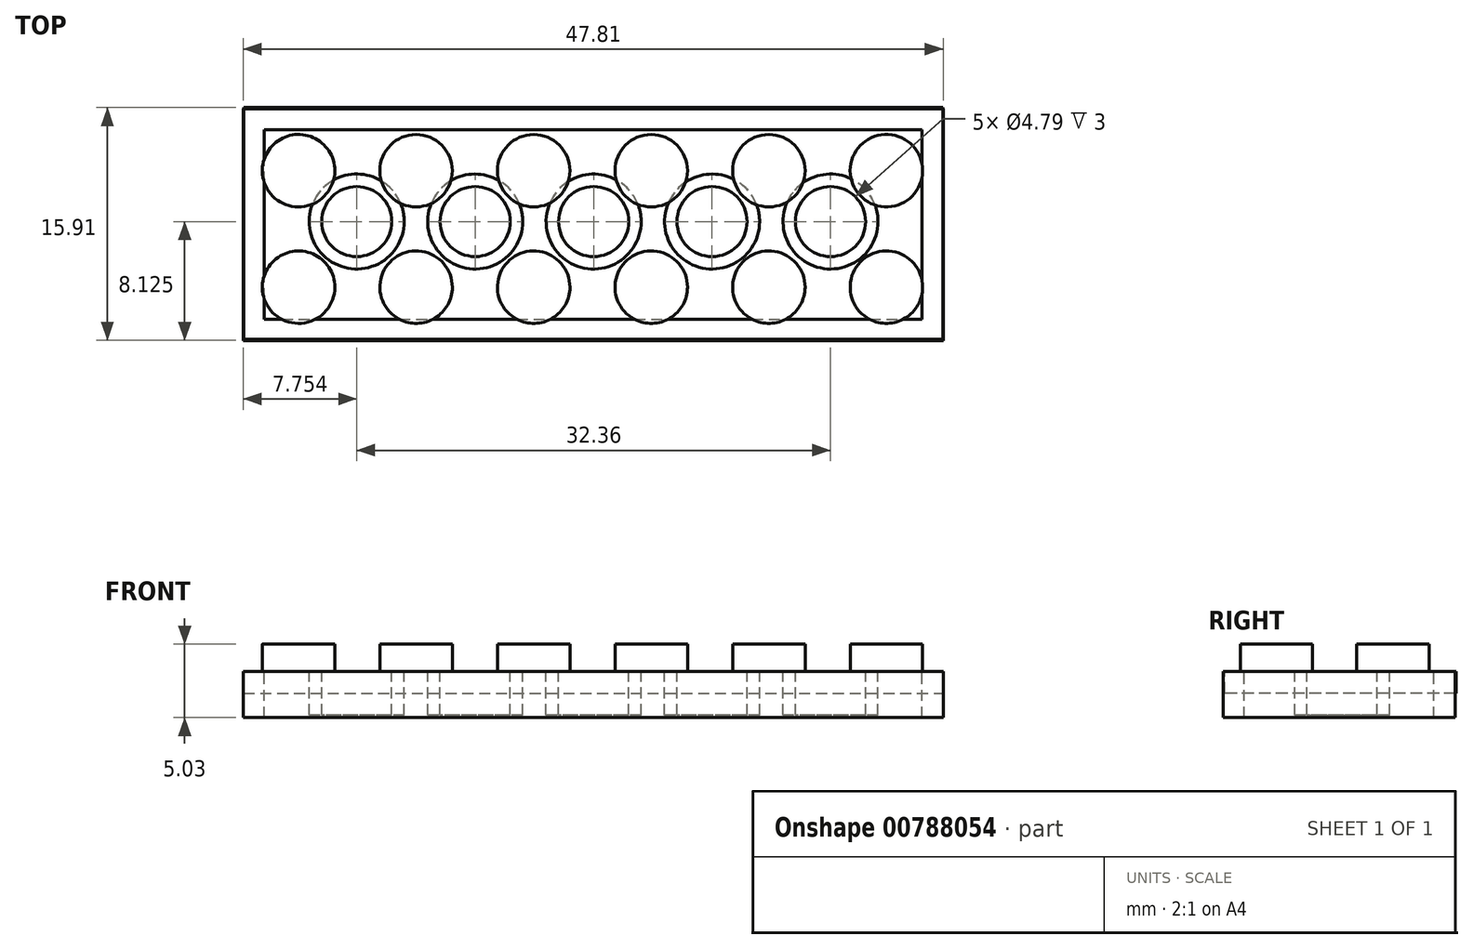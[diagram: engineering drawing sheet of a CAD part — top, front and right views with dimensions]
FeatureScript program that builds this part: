
annotation { "Feature Type Name" : "Feature", "Feature Type Description" : "" }
export const myFeature = defineFeature(function(context is Context, id is Id, definition is map)
    precondition{}
    {
        {
            var Q0;
            Q0=qCreatedBy(makeId("Top.planeOp"),FACE);
            var sketch = newSketch(context, id + "F0", { "sketchPlane" : qUnion([Q0])});
            skLineSegment(sketch, "E0.bottom", {"start": v(-44.16, 3.14) * mm, "end": v(3.65, 3.14) * mm});
            skLineSegment(sketch, "E0.top", {"start": v(-44.16, -12.7) * mm, "end": v(3.65, -12.7) * mm});
            skLineSegment(sketch, "E0.left", {"start": v(-44.16, 3.14) * mm, "end": v(-44.16, -12.7) * mm});
            skLineSegment(sketch, "E0.right", {"start": v(3.65, 3.14) * mm, "end": v(3.65, -12.7) * mm});
            skSolve(sketch);
        }
        {
            var Q0;
            Q0 = qSketchRegion(id + "F0", true);
            extrude(context, id + "F1", {"entities" : qUnion([Q0]), "oppositeDirection" : true, "depth" : 3.17 * mm, "offsetDistance" : 25 * mm});
        }
        {
            var Q0;
            Q0=qCreatedBy(makeId("Top.planeOp"),FACE);
            var sketch = newSketch(context, id + "F2", { "sketchPlane" : qUnion([Q0])});
            skCircle(sketch, "E1", {"center": v(-40.38, -1.1) * mm, "radius": 2.48 * mm});
            skCircle(sketch, "E2", {"center": v(-32.35, -1.1) * mm, "radius": 2.48 * mm});
            skCircle(sketch, "E3", {"center": v(-24.32, -1.1) * mm, "radius": 2.48 * mm});
            skCircle(sketch, "E4", {"center": v(-16.29, -1.1) * mm, "radius": 2.48 * mm});
            skCircle(sketch, "E5", {"center": v(-8.26, -1.1) * mm, "radius": 2.48 * mm});
            skCircle(sketch, "E6", {"center": v(-0.23, -1.1) * mm, "radius": 2.48 * mm});
            skCircle(sketch, "E7", {"center": v(-40.38, -9.06) * mm, "radius": 2.48 * mm});
            skCircle(sketch, "E8", {"center": v(-32.35, -9.06) * mm, "radius": 2.48 * mm});
            skCircle(sketch, "E9", {"center": v(-24.32, -9.06) * mm, "radius": 2.48 * mm});
            skCircle(sketch, "E10", {"center": v(-16.29, -9.06) * mm, "radius": 2.48 * mm});
            skCircle(sketch, "E11", {"center": v(-8.26, -9.06) * mm, "radius": 2.48 * mm});
            skCircle(sketch, "E12", {"center": v(-0.23, -9.06) * mm, "radius": 2.48 * mm});
            skSolve(sketch);
        }
        {
            var Q0;
            Q0 = qSketchRegion(id + "F2", true);
            extrude(context, id + "F3", {"entities" : qUnion([Q0]), "operationType" : NewBodyOperationType.ADD, "depth" : 1.86 * mm, "offsetDistance" : 25 * mm});
        }
        {
            var Q0;
            Q0=qCreatedBy(makeId("Top.planeOp"),FACE);
            var sketch = newSketch(context, id + "F4", { "sketchPlane" : qUnion([Q0])});
            skLineSegment(sketch, "E13.top", {"start": v(-42.71, -11.25) * mm, "end": v(2.2, -11.25) * mm});
            skLineSegment(sketch, "E14", {"start": v(-42.71, -11.25) * mm, "end": v(-42.71, 1.69) * mm});
            skLineSegment(sketch, "E15", {"start": v(-42.71, 1.69) * mm, "end": v(2.2, 1.69) * mm});
            skLineSegment(sketch, "E16", {"start": v(2.2, 1.69) * mm, "end": v(2.2, -11.25) * mm});
            skSolve(sketch);
        }
        {
            var Q0;
            Q0 = qSketchRegion(id + "F4", true);
            extrude(context, id + "F5", {"entities" : qUnion([Q0]), "operationType" : NewBodyOperationType.REMOVE, "oppositeDirection" : true, "depth" : 25 * mm, "offsetDistance" : 25 * mm});
        }
        {
            var Q0;
            Q0=qCreatedBy(makeId("Top.planeOp"),FACE);
            var sketch = newSketch(context, id + "F6", { "sketchPlane" : qUnion([Q0])});
            skLineSegment(sketch, "E17.bottom", {"start": v(-44.14, 3.2) * mm, "end": v(3.62, 3.2) * mm});
            skLineSegment(sketch, "E17.top", {"start": v(-44.14, -12.61) * mm, "end": v(3.62, -12.61) * mm});
            skLineSegment(sketch, "E17.left", {"start": v(-44.14, 3.2) * mm, "end": v(-44.14, -12.61) * mm});
            skLineSegment(sketch, "E17.right", {"start": v(3.62, 3.2) * mm, "end": v(3.62, -12.61) * mm});
            skSolve(sketch);
        }
        {
            var Q0;
            Q0 = qSketchRegion(id + "F6", true);
            extrude(context, id + "F7", {"entities" : qUnion([Q0]), "oppositeDirection" : true, "depth" : 1.5 * mm, "offsetDistance" : 25 * mm});
        }
        {
            var Q0;
            Q0=qCreatedBy(makeId("Top.planeOp"),FACE);
            var sketch = newSketch(context, id + "F8", { "sketchPlane" : qUnion([Q0])});
            skCircle(sketch, "E18", {"center": v(-36.4, -4.57) * mm, "radius": 3.25 * mm});
            skCircle(sketch, "E19", {"center": v(-28.32, -4.57) * mm, "radius": 3.25 * mm});
            skCircle(sketch, "E20", {"center": v(-20.23, -4.57) * mm, "radius": 3.25 * mm});
            skCircle(sketch, "E21", {"center": v(-12.14, -4.57) * mm, "radius": 3.25 * mm});
            skCircle(sketch, "E22", {"center": v(-4.05, -4.57) * mm, "radius": 3.25 * mm});
            skCircle(sketch, "E23", {"center": v(-36.4, -4.57) * mm, "radius": 2.4 * mm});
            skCircle(sketch, "E24", {"center": v(-28.32, -4.57) * mm, "radius": 2.4 * mm});
            skCircle(sketch, "E25", {"center": v(-20.23, -4.57) * mm, "radius": 2.4 * mm});
            skCircle(sketch, "E26", {"center": v(-12.14, -4.57) * mm, "radius": 2.4 * mm});
            skCircle(sketch, "E27", {"center": v(-4.05, -4.57) * mm, "radius": 2.4 * mm});
            skSolve(sketch);
        }
        {
            var Q0;
            Q0 = qSketchRegion(id + "F8", true);
            extrude(context, id + "F9", {"entities" : qUnion([Q0]), "oppositeDirection" : true, "depth" : 3 * mm, "offsetDistance" : 25 * mm});
        }
    });
